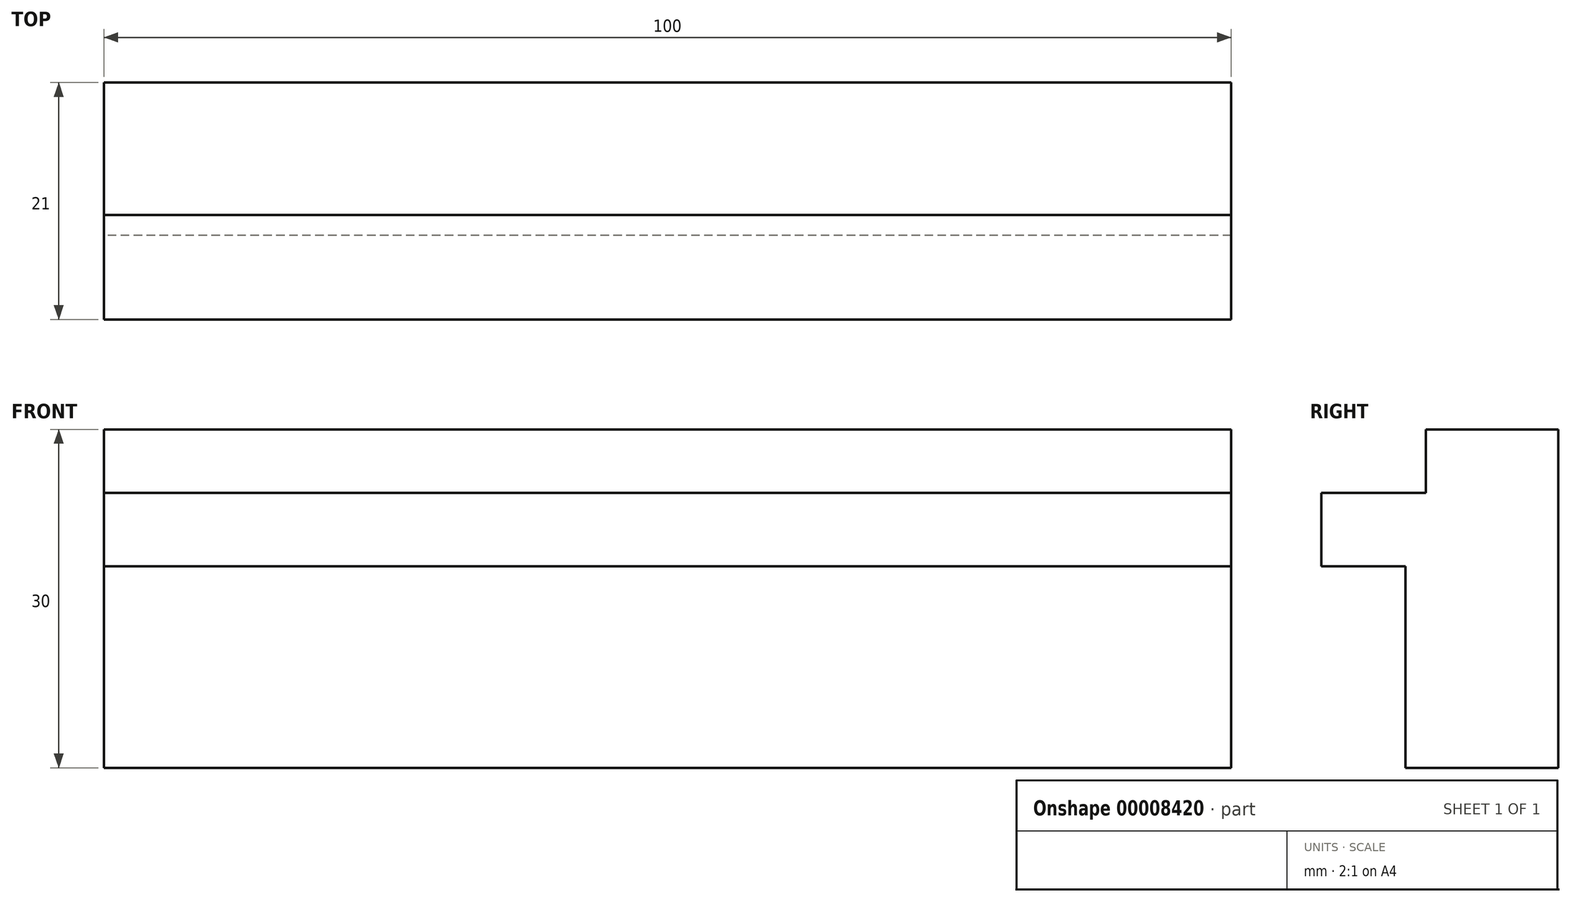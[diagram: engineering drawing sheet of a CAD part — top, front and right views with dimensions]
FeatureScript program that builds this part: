
annotation { "Feature Type Name" : "Feature", "Feature Type Description" : "" }
export const myFeature = defineFeature(function(context is Context, id is Id, definition is map)
    precondition{}
    {
        {
            var Q0;
            Q0=qCreatedBy(makeId("Right.planeOp"),FACE);
            var sketch = newSketch(context, id + "F0", { "sketchPlane" : qUnion([Q0])});
            skLineSegment(sketch, "E0", {"start": v(-8.84, -15.6) * mm, "end": v(-8.84, 14.4) * mm});
            skLineSegment(sketch, "E1", {"start": v(-8.84, 14.4) * mm, "end": v(-20.6, 14.4) * mm});
            skLineSegment(sketch, "E2", {"start": v(-20.6, 14.4) * mm, "end": v(-20.6, 8.77) * mm});
            skLineSegment(sketch, "E3", {"start": v(-20.6, 8.77) * mm, "end": v(-29.84, 8.77) * mm});
            skLineSegment(sketch, "E4", {"start": v(-29.84, 8.77) * mm, "end": v(-29.84, 2.27) * mm});
            skLineSegment(sketch, "E5", {"start": v(-29.84, 2.27) * mm, "end": v(-22.38, 2.27) * mm});
            skLineSegment(sketch, "E6", {"start": v(-22.38, 2.27) * mm, "end": v(-22.38, -15.6) * mm});
            skLineSegment(sketch, "E7", {"start": v(-22.38, -15.6) * mm, "end": v(-8.84, -15.6) * mm});
            skSolve(sketch);
        }
        {
            var Q0;
            Q0 = qSketchRegion(id + "F0", true);
            extrude(context, id + "F1", {"entities" : qUnion([Q0]), "depth" : 100 * mm});
        }
    });
